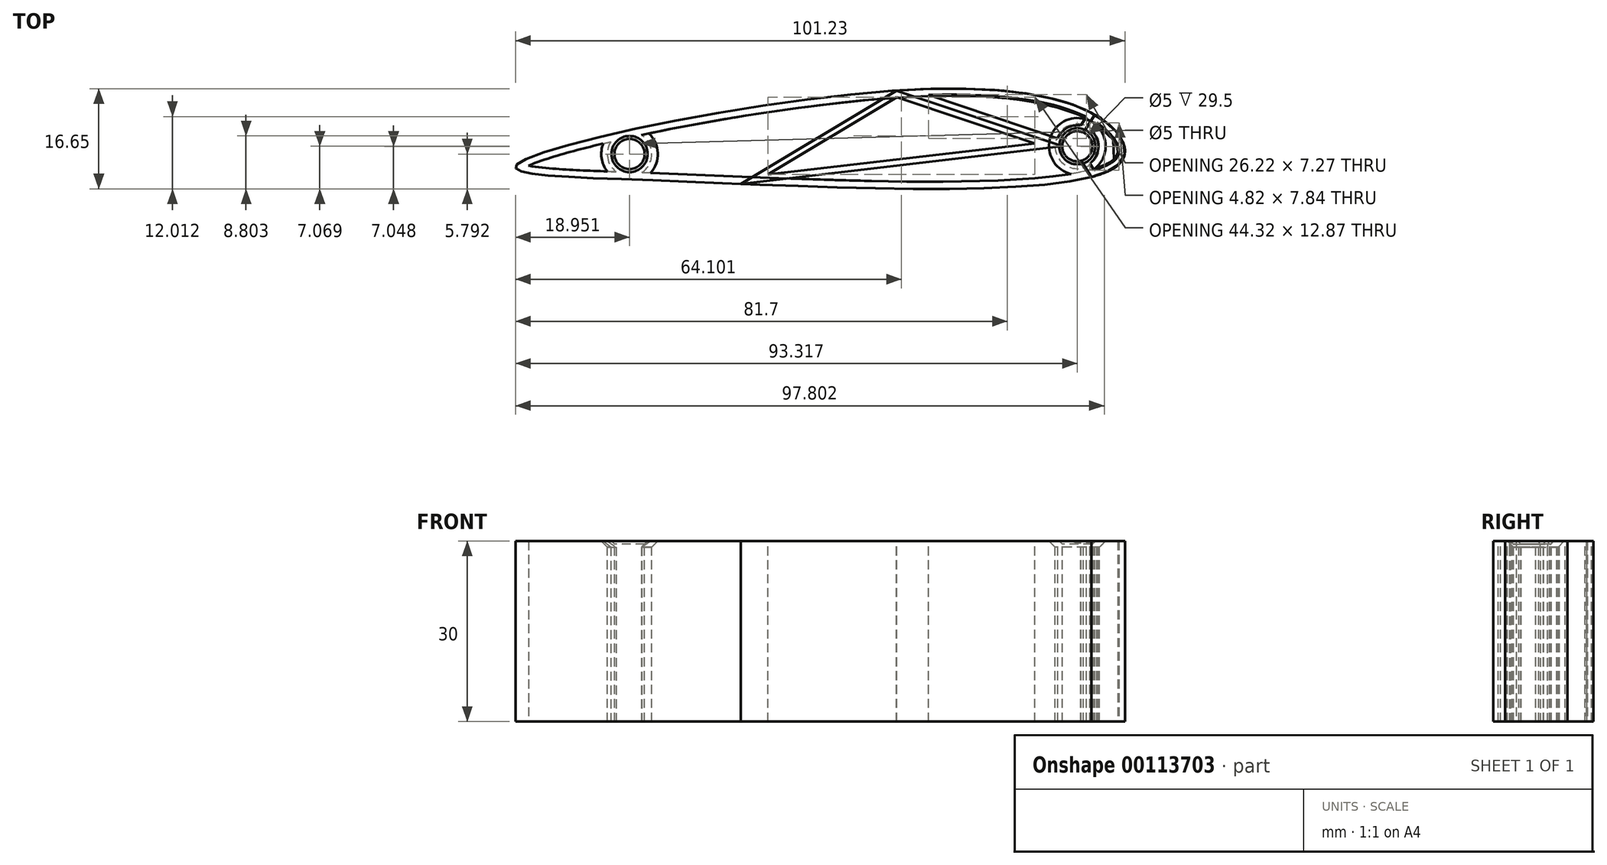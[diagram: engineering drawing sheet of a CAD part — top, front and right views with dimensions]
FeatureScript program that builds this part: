
annotation { "Feature Type Name" : "Feature", "Feature Type Description" : "" }
export const myFeature = defineFeature(function(context is Context, id is Id, definition is map)
    precondition{}
    {
        {
            var Q0;
            Q0=qCreatedBy(makeId("Top.planeOp"),FACE);
            var sketch = newSketch(context, id + "F0", { "sketchPlane" : qUnion([Q0])});
            skLineSegment(sketch, "E0", {"start": v(-52.13, 0) * mm, "end": v(47.87, 0) * mm});
            skFitSpline(sketch, "E1", {"points": [v(-52.13, 0) * mm, v(11.32, 12.34) * mm, v(46.56, 6.4) * mm, v(47.87, 0) * mm, v(-27.08, -2.69) * mm, v(-52.13, 0) * mm]});
            skSolve(sketch);
        }
        {
            var Q0;
            Q0 = qSketchRegion(id + "F0", true);
            extrude(context, id + "F1", {"entities" : qUnion([Q0]), "depth" : 30 * mm});
        }
        {
            var Q0;
            Q0=makeQuery(id+"F1.opExtrude","CAP_FACE",FACE,{"disambiguationData":[OSD([sQuery(id+"F0.wireOp",EDGE,"E1")])],"isStart":false});
            var sketch = newSketch(context, id + "F2", { "sketchPlane" : qUnion([Q0])});
            skCircle(sketch, "E2", {"center": v(41, 3.05) * mm, "radius": 2.5 * mm});
            skCircle(sketch, "E3", {"center": v(-33.37, 1.77) * mm, "radius": 2.5 * mm});
            skLineSegment(sketch, "E4", {"start": v(38.5, 3.05) * mm, "end": v(10.92, 12.31) * mm});
            skLineSegment(sketch, "E5", {"start": v(10.92, 12.31) * mm, "end": v(-14.87, -3.18) * mm});
            skLineSegment(sketch, "E6", {"start": v(-14.87, -3.18) * mm, "end": v(-30.88, 2.03) * mm});
            skLineSegment(sketch, "E7", {"start": v(-33.13, -0.72) * mm, "end": v(-33.13, -2.47) * mm});
            skLineSegment(sketch, "E8", {"start": v(-33.74, 4.24) * mm, "end": v(-33.74, 5.65) * mm});
            skLineSegment(sketch, "E9", {"start": v(42, 5.34) * mm, "end": v(43.92, 8.31) * mm});
            skLineSegment(sketch, "E10", {"start": v(41.65, 0.63) * mm, "end": v(43.31, -2.06) * mm});
            skLineSegment(sketch, "E11", {"start": v(38.5, 3.05) * mm, "end": v(-14.87, -3.18) * mm});
            skLineSegment(sketch, "E12", {"start": v(10.92, 12.31) * mm, "end": v(-30.88, 2.03) * mm});
            skSolve(sketch);
        }
        {
            var Q0;
            Q0=sQuery(id+"F2.wireOp",VERTEX,"E2.center");
            var Q1;
            Q1=makeQuery(id+"F1.opExtrude","SWEPT_BODY",BODY,{"disambiguationData":[OSD([sQuery(id+"F0.wireOp",EDGE,"E1")])]});
            hole(context, id + "F3", {"style" : HoleStyle.C_SINK, "endStyle" : HoleEndStyle.THROUGH, "holeDiameter" : 5 * mm, "cSinkDiameter" : 6 * mm, "cSinkAngle" : 90 * degree, "locations" : qUnion([Q0]), "scope" : qUnion([Q1]), "isTappedThrough" : true});
        }
        {
            var Q0;
            Q0=sQuery(id+"F2.wireOp",VERTEX,"E3.center");
            var Q1;
            Q1=makeQuery(id+"F1.opExtrude","SWEPT_BODY",BODY,{"disambiguationData":[OSD([sQuery(id+"F0.wireOp",EDGE,"E1")])]});
            hole(context, id + "F4", {"style" : HoleStyle.C_SINK, "endStyle" : HoleEndStyle.THROUGH, "holeDiameter" : 5 * mm, "cSinkDiameter" : 6 * mm, "cSinkAngle" : 90 * degree, "locations" : qUnion([Q0]), "scope" : qUnion([Q1]), "isTappedThrough" : true});
        }
        {
            var Q0;
            Q0=makeQuery(id+"F1.opExtrude","CAP_FACE",FACE,{"disambiguationData":[OSD([sQuery(id+"F0.wireOp",EDGE,"E1")])],"isStart":false});
            var Q1;
            Q1=makeQuery(id+"F1.opExtrude","CAP_FACE",FACE,{"disambiguationData":[OSD([sQuery(id+"F0.wireOp",EDGE,"E1")])],"isStart":true});
            shell(context, id + "F5", {"entities" : qUnion([Q0, Q1]), "thickness" : 1.2 * mm});
        }
        {
            var Q0;
            {var subQ0=sQuery(id+"F2.wireOp",EDGE,"E4");Q0=makeQuery(id+"F2.imprint","IMPRINT",FACE,{"disambiguationData":[TD([[makeQuery(id+"F2.imprint","IMPRINT",EDGE,{"derivedFrom":subQ0}),-1.0]])]});}
            extrude(context, id + "F6", {"entities" : qUnion([Q0]), "oppositeDirection" : true, "depth" : 30 * mm});
        }
        {
            var Q0;
            Q0=makeQuery(id+"F6.opExtrude","CAP_FACE",FACE,{"disambiguationData":[OSD([sQuery(id+"F0.wireOp",EDGE,"E1"),sQuery(id+"F2.wireOp",EDGE,"E2"),sQuery(id+"F2.wireOp",EDGE,"E4"),sQuery(id+"F2.wireOp",EDGE,"E9")])],"isStart":false});
            var Q1;
            Q1=makeQuery(id+"F6.opExtrude","CAP_FACE",FACE,{"disambiguationData":[OSD([sQuery(id+"F0.wireOp",EDGE,"E1"),sQuery(id+"F2.wireOp",EDGE,"E2"),sQuery(id+"F2.wireOp",EDGE,"E4"),sQuery(id+"F2.wireOp",EDGE,"E9")])],"isStart":true});
            shell(context, id + "F7", {"entities" : qUnion([Q0, Q1]), "thickness" : 1 * mm});
        }
        {
            var Q0;
            Q0=makeQuery(id+"F2.imprint","IMPRINT",FACE,{"disambiguationData":[TD([[makeQuery(id+"F2.imprint","IMPRINT",EDGE,{"derivedFrom":sQuery(id+"F2.wireOp",EDGE,"E4")}),1.0]])]});
            extrude(context, id + "F8", {"entities" : qUnion([Q0]), "oppositeDirection" : true, "depth" : 30 * mm});
        }
        {
            var Q0;
            Q0=makeQuery(id+"F8.opExtrude","CAP_FACE",FACE,{"disambiguationData":[OSD([sQuery(id+"F2.wireOp",EDGE,"E4"),sQuery(id+"F2.wireOp",EDGE,"E5"),sQuery(id+"F2.wireOp",EDGE,"E11")])],"isStart":true});
            var Q1;
            Q1=makeQuery(id+"F8.opExtrude","CAP_FACE",FACE,{"disambiguationData":[OSD([sQuery(id+"F2.wireOp",EDGE,"E4"),sQuery(id+"F2.wireOp",EDGE,"E5"),sQuery(id+"F2.wireOp",EDGE,"E11")])],"isStart":false});
            shell(context, id + "F9", {"entities" : qUnion([Q0, Q1]), "thickness" : 1 * mm});
        }
        {
            var Q0;
            {var subQ0=sQuery(id+"F2.wireOp",EDGE,"E9");Q0=makeQuery(id+"F2.imprint","IMPRINT",FACE,{"disambiguationData":[TD([[makeQuery(id+"F2.imprint","IMPRINT",EDGE,{"derivedFrom":subQ0}),-1.0]])]});}
            extrude(context, id + "F10", {"entities" : qUnion([Q0]), "oppositeDirection" : true, "depth" : 30 * mm});
        }
        {
            var Q0;
            Q0=makeQuery(id+"F10.opExtrude","CAP_FACE",FACE,{"disambiguationData":[OSD([sQuery(id+"F0.wireOp",EDGE,"E1"),sQuery(id+"F2.wireOp",EDGE,"E2"),sQuery(id+"F2.wireOp",EDGE,"E9"),sQuery(id+"F2.wireOp",EDGE,"E10")])],"isStart":true});
            var Q1;
            Q1=makeQuery(id+"F10.opExtrude","CAP_FACE",FACE,{"disambiguationData":[OSD([sQuery(id+"F0.wireOp",EDGE,"E1"),sQuery(id+"F2.wireOp",EDGE,"E2"),sQuery(id+"F2.wireOp",EDGE,"E9"),sQuery(id+"F2.wireOp",EDGE,"E10")])],"isStart":false});
            shell(context, id + "F11", {"entities" : qUnion([Q0, Q1]), "thickness" : 1 * mm});
        }
    });
